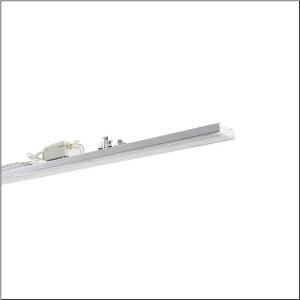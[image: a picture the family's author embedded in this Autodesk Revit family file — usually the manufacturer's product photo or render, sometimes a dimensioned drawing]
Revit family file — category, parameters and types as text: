
# Revit family: licross_11_recessed_mo_51tl1e7n485g
name_source: partatom
category: Lighting Fixtures
units: mm (PartAtom-declared; Revit-internal decimal feet)

## family parameters
Cut with Voids When Loaded = No
Host = Face
Light Source = No
Part Type = Normal
Room Calculation Point = No
Round Connector Dimension = Use Diameter
Shared = No

## types (1)
- Licross 11 Recessed MO (1 x LED, 8660 lm, 48.5 W, 4000K)
    Apparent Load = 49 VA
    CIE Flux Codes = 85 95 99 100 100
    Color Rendering = 80
    Color Temperature = 4000K
    Default Elevation = 1800 mm
    Description = Licross 11 Recessed MO, luminaire insert, of sheet steel, coil coated, white, length: 1.500mm, width: 66mm, height: 67mm, LED rated luminous flux: 8.660lm, light colour: 840, SDCM (Standard Deviation of Colour Matching)MacAdam ≤ 2 SDCM (initial), control gear: ON/OFF, with plug, 3-pole, with phase selection, mains connection: 220..240V, AC, 50/60Hz, rated input power: 49W, internal wiring halogen-free, primary light control with lens, of plastic, primary optical cover: cover, of PMMA, light emission: direct distribution, primary light characteristic: symmetric, protection rating (complete): IP40, insulation class (complete): insulation class I (protective earthing), certification: CE, ENEC, VDE, UKCA, protection symbol: D if used in an environment without relevant dust loads with corresponding accessories, impact resistance: IK06, permissible ambient temperature for indoor applications: -35..+35°C, corresponds to IFS (International Featured Standards) requirements for safety and quality in the food industry, reducing of maximum allowable ambient temperature of 5°C with ceiling mounting, The light source and the operating device comply with the requirements of the Ecodesign Regulation (EU) 2019/2020 and are replaceable in accordance with this regulation, packaging unit: 1 piece
    Height = 58 mm
    Lamp = 1 x LED
    Lamp Light Flux = 8660 lm
    Lamp Power = 48.5 W
    Lamp count = 1
    Length = 1500 mm
    Luminous efficacy = 179 lm/W
    Manufacturer = Siteco
    ModVariant = No
    Model = 51TL1E7N485G
    Mounting Place = Ceiling
    Mounting Type = Pendant
    Number of Poles = 1
    OnlyDefault = Yes
    Power Factor = 1
    Product Name = Licross 11 Recessed MO
    Product group = luminaire insert | ceiling pendant
    ProductGroupID = 901
    Protection Class = Protection class I
    Protection Degree = IP 40
    RLX_Detail_Level = 1
    RLX_Emergency_Light_Flux = 0 lm
    RLX_Emergency_Type = 0
    RLX_Emergency_Type_DB = No
    RlxData = <blob elided: 21177 chars, md5=7f20c737>
    Socket = socket
    Standby Power = 0 W
    System Light Flux = 8660 lm
    System Power = 49 W
    Type Comments = Product without accessories
    Type Image = l_1296930.jpg
    URL = http://relux.com
    VarID = ---
    Voltage = 0 V
    Weight = 0.00 kg
    Width = 66 mm

## geometry (parser evidence)
native form markers: Blend x4, Sweep x10
no freeform markers — native parametric forms only
